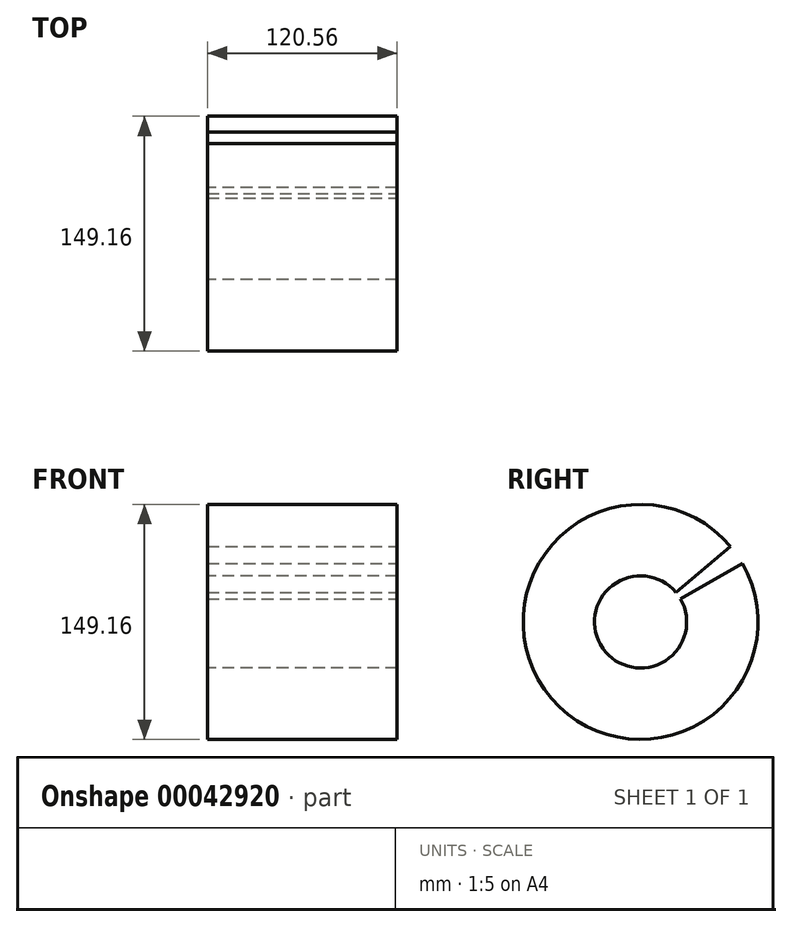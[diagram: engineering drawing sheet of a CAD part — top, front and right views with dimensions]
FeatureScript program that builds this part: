
annotation { "Feature Type Name" : "Feature", "Feature Type Description" : "" }
export const myFeature = defineFeature(function(context is Context, id is Id, definition is map)
    precondition{}
    {
        {
            var Q0;
            Q0=qCreatedBy(makeId("Top.planeOp"),FACE);
            var sketch = newSketch(context, id + "F0", { "sketchPlane" : qUnion([Q0])});
            skLineSegment(sketch, "E0.bottom", {"start": v(-54.96, 0) * mm, "end": v(65.6, 0) * mm});
            skLineSegment(sketch, "E0.top", {"start": v(-54.96, 45.3) * mm, "end": v(65.6, 45.3) * mm});
            skLineSegment(sketch, "E0.left", {"start": v(-54.96, 0) * mm, "end": v(-54.96, 45.3) * mm});
            skLineSegment(sketch, "E0.right", {"start": v(65.6, 0) * mm, "end": v(65.6, 45.3) * mm});
            skLineSegment(sketch, "E1", {"start": v(-65.87, -29.28) * mm, "end": v(85, -29.28) * mm});
            skSolve(sketch);
        }
        {
            var Q0;
            Q0=makeQuery(id+"F0.imprint","IMPRINT",FACE,{"disambiguationData":[TD([[makeQuery(id+"F0.imprint","IMPRINT",EDGE,{"derivedFrom":sQuery(id+"F0.wireOp",EDGE,"E0.bottom")}),1.0]])]});
            var Q1;
            Q1=sQuery(id+"F0.wireOp",EDGE,"E1");
            revolve(context, id + "F1", {"entities" : qUnion([Q0]), "axis" : qUnion([Q1]), "revolveType" : RevolveType.TWO_DIRECTIONS, "angle" : 30 * degree, "angleBack" : 40 * degree});
        }
    });
